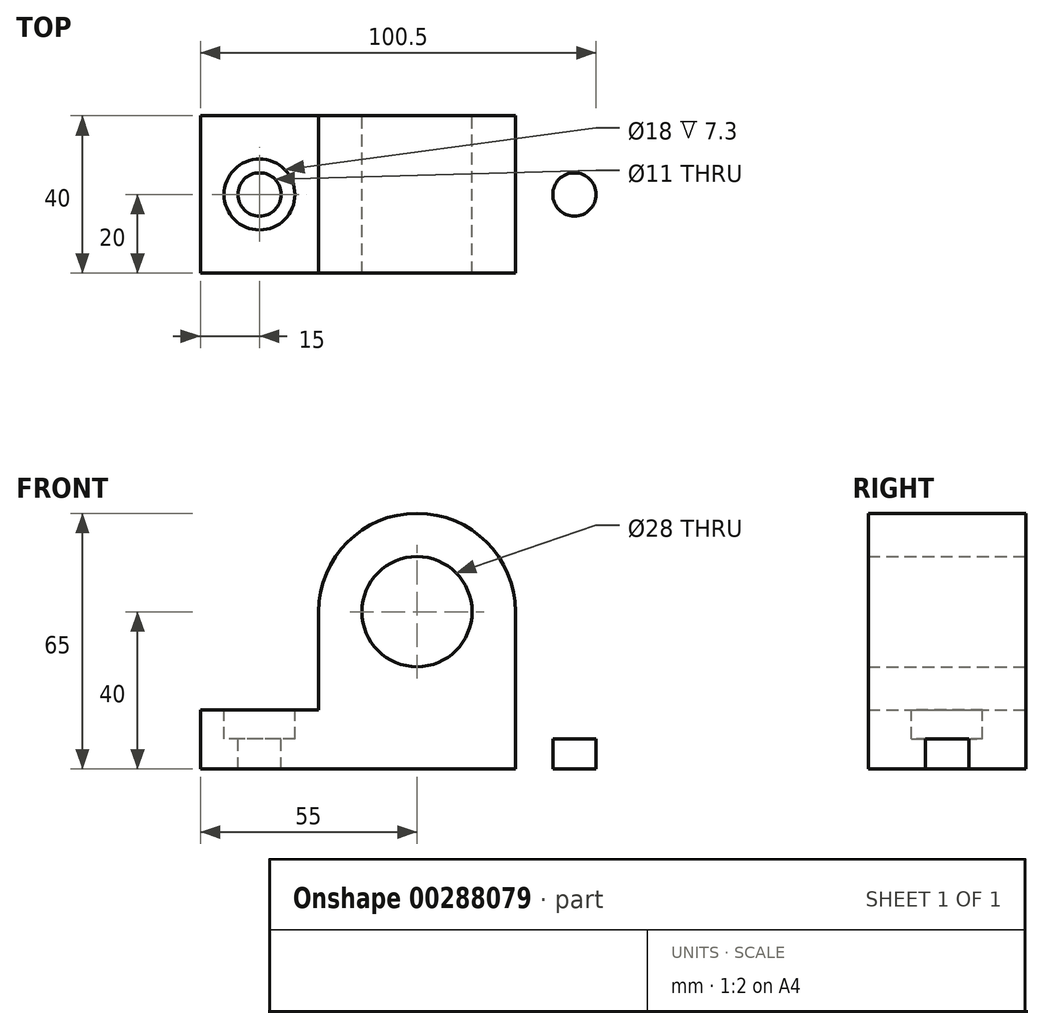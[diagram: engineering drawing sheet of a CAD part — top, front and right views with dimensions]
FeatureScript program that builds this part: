
annotation { "Feature Type Name" : "Feature", "Feature Type Description" : "" }
export const myFeature = defineFeature(function(context is Context, id is Id, definition is map)
    precondition{}
    {
        {
            var Q0;
            Q0=qCreatedBy(makeId("Front.planeOp"),FACE);
            var sketch = newSketch(context, id + "F0", { "sketchPlane" : qUnion([Q0])});
            skLineSegment(sketch, "E0", {"start": v(-55, 15) * mm, "end": v(-25, 15) * mm});
            skLineSegment(sketch, "E1", {"start": v(-25, 15) * mm, "end": v(-25, 40) * mm});
            skLineSegment(sketch, "E2", {"start": v(0, 65) * mm, "end": v(0, 65) * mm});
            skLineSegment(sketch, "E3", {"start": v(25, 40) * mm, "end": v(25, 15) * mm});
            skLineSegment(sketch, "E4", {"start": v(25, 15) * mm, "end": v(55, 15) * mm});
            skLineSegment(sketch, "E5", {"start": v(55, 15) * mm, "end": v(55, 0) * mm});
            skLineSegment(sketch, "E6", {"start": v(55, 0) * mm, "end": v(-55, 0) * mm});
            skLineSegment(sketch, "E7", {"start": v(-55, 0) * mm, "end": v(-55, 15) * mm});
            skCircle(sketch, "E8", {"center": v(0, 40) * mm, "radius": 14 * mm});
            skLineSegment(sketch, "E9", {"start": v(-49, 15) * mm, "end": v(-49, 7.7) * mm});
            skLineSegment(sketch, "E10", {"start": v(-49, 7.7) * mm, "end": v(-31, 7.7) * mm});
            skLineSegment(sketch, "E11", {"start": v(-31, 7.7) * mm, "end": v(-31, 15) * mm});
            skLineSegment(sketch, "E12", {"start": v(-45.5, 7.7) * mm, "end": v(-45.5, 0) * mm});
            skLineSegment(sketch, "E13", {"start": v(-34.5, 7.7) * mm, "end": v(-34.5, 0) * mm});
            skLineSegment(sketch, "E14.MirrorCS", {"start": v(49, 15) * mm, "end": v(49, 7.7) * mm});
            skLineSegment(sketch, "E15.MirrorCS", {"start": v(31, 7.7) * mm, "end": v(31, 15) * mm});
            skLineSegment(sketch, "E16.MirrorCS", {"start": v(49, 7.7) * mm, "end": v(31, 7.7) * mm});
            skLineSegment(sketch, "E17.MirrorCS", {"start": v(45.5, 7.7) * mm, "end": v(45.5, 0) * mm});
            skLineSegment(sketch, "E18.MirrorCS", {"start": v(34.5, 7.7) * mm, "end": v(34.5, 0) * mm});
            skPoint(sketch, "E19.visualSharp", {"position": v(-25, 65) * mm});
            skArc(sketch, "E19.filletArc", {"start": v(0, 65) * mm, "mid": v(-17.68, 57.68) * mm, "end": v(-25, 40) * mm});
            skPoint(sketch, "E20.visualSharp", {"position": v(25, 65) * mm});
            skArc(sketch, "E20.filletArc", {"start": v(25, 40) * mm, "mid": v(17.68, 57.68) * mm, "end": v(0, 65) * mm});
            skPoint(sketch, "E21.end.orphan", {"position": v(-40, 0) * mm});
            skSolve(sketch);
        }
        {
            var Q0;
            Q0 = qSketchRegion(id + "F0", true);
            extrude(context, id + "F1", {"entities" : qUnion([Q0]), "endBound" : BoundingType.SYMMETRIC, "depth" : 40 * mm});
        }
        {
            var Q0;
            Q0=makeQuery(id+"F1.opExtrude","SWEPT_FACE",FACE,{"disambiguationData":[OSD([sQuery(id+"F0.wireOp",EDGE,"E0")])]});
            var sketch = newSketch(context, id + "F2", { "sketchPlane" : qUnion([Q0])});
            skCircle(sketch, "E22", {"center": v(-40, 0) * mm, "radius": 9 * mm});
            skCircle(sketch, "E23", {"center": v(-40, 0) * mm, "radius": 5.5 * mm});
            skCircle(sketch, "E24.MirrorC", {"center": v(40, 0) * mm, "radius": 5.5 * mm});
            skCircle(sketch, "E25.MirrorC", {"center": v(40, 0) * mm, "radius": 9 * mm});
            skSolve(sketch);
        }
        {
            var Q0;
            Q0=makeQuery(id+"F2.imprint","IMPRINT",FACE,{"disambiguationData":[TD([[makeQuery(id+"F2.imprint","IMPRINT",EDGE,{"derivedFrom":sQuery(id+"F2.wireOp",EDGE,"E22")}),1.0]])]});
            var Q1;
            Q1=makeQuery(id+"F2.imprint","IMPRINT",FACE,{"disambiguationData":[TD([[makeQuery(id+"F2.imprint","IMPRINT",EDGE,{"derivedFrom":sQuery(id+"F2.wireOp",EDGE,"E24.MirrorC")}),1.0]])]});
            var Q2;
            Q2=sQuery(id+"F2.wireOp",EDGE,"E23");
            var Q3;
            Q3=sQuery(id+"F2.wireOp",EDGE,"E24.MirrorC");
            extrude(context, id + "F3", {"entities" : qUnion([Q0, Q1]), "operationType" : NewBodyOperationType.REMOVE, "surfaceEntities" : qUnion([Q2, Q3]), "oppositeDirection" : true, "depth" : 7.3 * mm});
        }
        {
            var Q0;
            Q0=makeQuery(id+"F3.boolean.opBoolean","SPLIT",FACE,{"disambiguationData":[TD([makeQuery(id+"F3.opExtrude","SWEPT_FACE",FACE,{"disambiguationData":[OSD([sQuery(id+"F2.wireOp",EDGE,"E23")])]})])],"derivedFrom":makeQuery(id+"F1.opExtrude","SWEPT_FACE",FACE,{"disambiguationData":[OSD([sQuery(id+"F0.wireOp",EDGE,"E0")])]})});
            var Q1;
            Q1=makeQuery(id+"F3.boolean.opBoolean","SPLIT",FACE,{"disambiguationData":[TD([makeQuery(id+"F3.opExtrude","SWEPT_FACE",FACE,{"disambiguationData":[OSD([sQuery(id+"F2.wireOp",EDGE,"E24.MirrorC")])]})])],"derivedFrom":makeQuery(id+"F1.opExtrude","SWEPT_FACE",FACE,{"disambiguationData":[OSD([sQuery(id+"F0.wireOp",EDGE,"E4")])]})});
            var Q2;
            Q2=sQuery(id+"F2.wireOp",EDGE,"E23");
            var Q3;
            Q3=sQuery(id+"F2.wireOp",EDGE,"E24.MirrorC");
            extrude(context, id + "F4", {"entities" : qUnion([Q0, Q1]), "operationType" : NewBodyOperationType.REMOVE, "surfaceEntities" : qUnion([Q2, Q3]), "oppositeDirection" : true, "depth" : 15 * mm});
        }
    });
